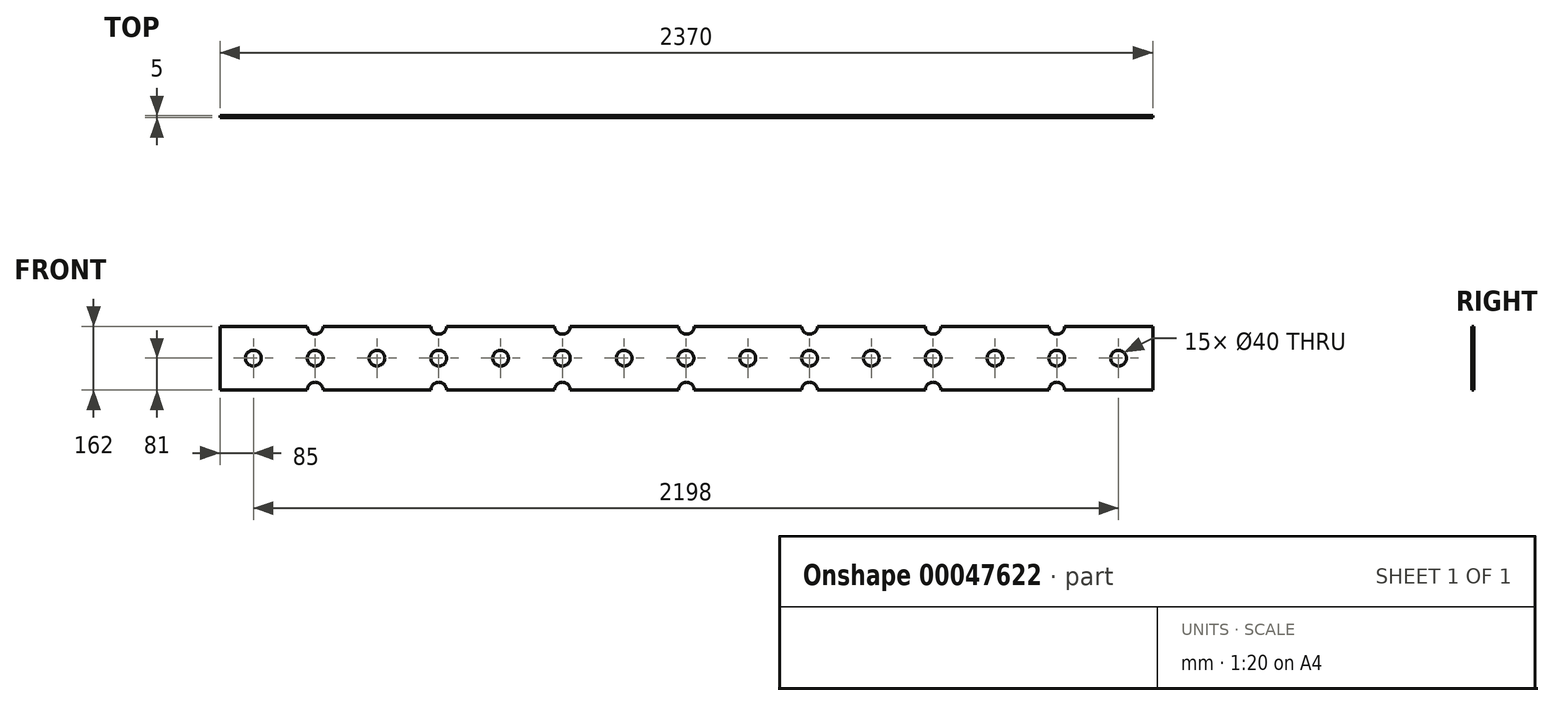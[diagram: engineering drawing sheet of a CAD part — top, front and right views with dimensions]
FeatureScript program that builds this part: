
annotation { "Feature Type Name" : "Feature", "Feature Type Description" : "" }
export const myFeature = defineFeature(function(context is Context, id is Id, definition is map)
    precondition{}
    {
        {
            var Q0;
            Q0=qCreatedBy(makeId("Front.planeOp"),FACE);
            var sketch = newSketch(context, id + "F0", { "sketchPlane" : qUnion([Q0])});
            skLineSegment(sketch, "E0.bottom", {"start": v(0, 0) * mm, "end": v(2370, 0) * mm});
            skLineSegment(sketch, "E0.top", {"start": v(0, 162) * mm, "end": v(2370, 162) * mm});
            skLineSegment(sketch, "E0.left", {"start": v(0, 0) * mm, "end": v(0, 162) * mm});
            skLineSegment(sketch, "E0.right", {"start": v(2370, 0) * mm, "end": v(2370, 162) * mm});
            skCircle(sketch, "E1", {"center": v(85, 81) * mm, "radius": 20 * mm});
            skCircle(sketch, "E2", {"center": v(242, 81) * mm, "radius": 20 * mm});
            skCircle(sketch, "E3", {"center": v(399, 81) * mm, "radius": 20 * mm});
            skCircle(sketch, "E4", {"center": v(556, 81) * mm, "radius": 20 * mm});
            skCircle(sketch, "E5", {"center": v(713, 81) * mm, "radius": 20 * mm});
            skCircle(sketch, "E6", {"center": v(870, 81) * mm, "radius": 20 * mm});
            skCircle(sketch, "E7", {"center": v(1027, 81) * mm, "radius": 20 * mm});
            skCircle(sketch, "E8", {"center": v(1184, 81) * mm, "radius": 20 * mm});
            skCircle(sketch, "E9", {"center": v(1341, 81) * mm, "radius": 20 * mm});
            skCircle(sketch, "E10", {"center": v(1498, 81) * mm, "radius": 20 * mm});
            skCircle(sketch, "E11", {"center": v(1655, 81) * mm, "radius": 20 * mm});
            skCircle(sketch, "E12", {"center": v(1812, 81) * mm, "radius": 20 * mm});
            skCircle(sketch, "E13", {"center": v(1969, 81) * mm, "radius": 20 * mm});
            skCircle(sketch, "E14", {"center": v(2126, 81) * mm, "radius": 20 * mm});
            skCircle(sketch, "E15", {"center": v(2283, 81) * mm, "radius": 20 * mm});
            skCircle(sketch, "E16", {"center": v(242, 162) * mm, "radius": 20 * mm});
            skCircle(sketch, "E17", {"center": v(556, 162) * mm, "radius": 20 * mm});
            skCircle(sketch, "E18", {"center": v(870, 162) * mm, "radius": 20 * mm});
            skCircle(sketch, "E19", {"center": v(1185, 162) * mm, "radius": 20 * mm});
            skCircle(sketch, "E20", {"center": v(242, 0) * mm, "radius": 20 * mm});
            skCircle(sketch, "E21", {"center": v(556, 0) * mm, "radius": 20 * mm});
            skCircle(sketch, "E22", {"center": v(870, 0) * mm, "radius": 20 * mm});
            skCircle(sketch, "E23", {"center": v(1185, 0) * mm, "radius": 20 * mm});
            skCircle(sketch, "E24", {"center": v(1498, 0) * mm, "radius": 20 * mm});
            skCircle(sketch, "E25", {"center": v(1498, 162) * mm, "radius": 20 * mm});
            skCircle(sketch, "E26", {"center": v(1812, 162) * mm, "radius": 20 * mm});
            skCircle(sketch, "E27", {"center": v(1812, 0) * mm, "radius": 20 * mm});
            skCircle(sketch, "E28", {"center": v(2126, 0) * mm, "radius": 20 * mm});
            skCircle(sketch, "E29", {"center": v(2126, 162) * mm, "radius": 20 * mm});
            skSolve(sketch);
        }
        {
            var Q0;
            {var subQ14=sQuery(id+"F0.wireOp",EDGE,"E0.left");Q0=makeQuery(id+"F0.imprint","IMPRINT",FACE,{"disambiguationData":[TD([[makeQuery(id+"F0.imprint","IMPRINT",EDGE,{"derivedFrom":subQ14}),-1.0]])]});}
            extrude(context, id + "F1", {"entities" : qUnion([Q0]), "depth" : 5 * mm});
        }
    });
